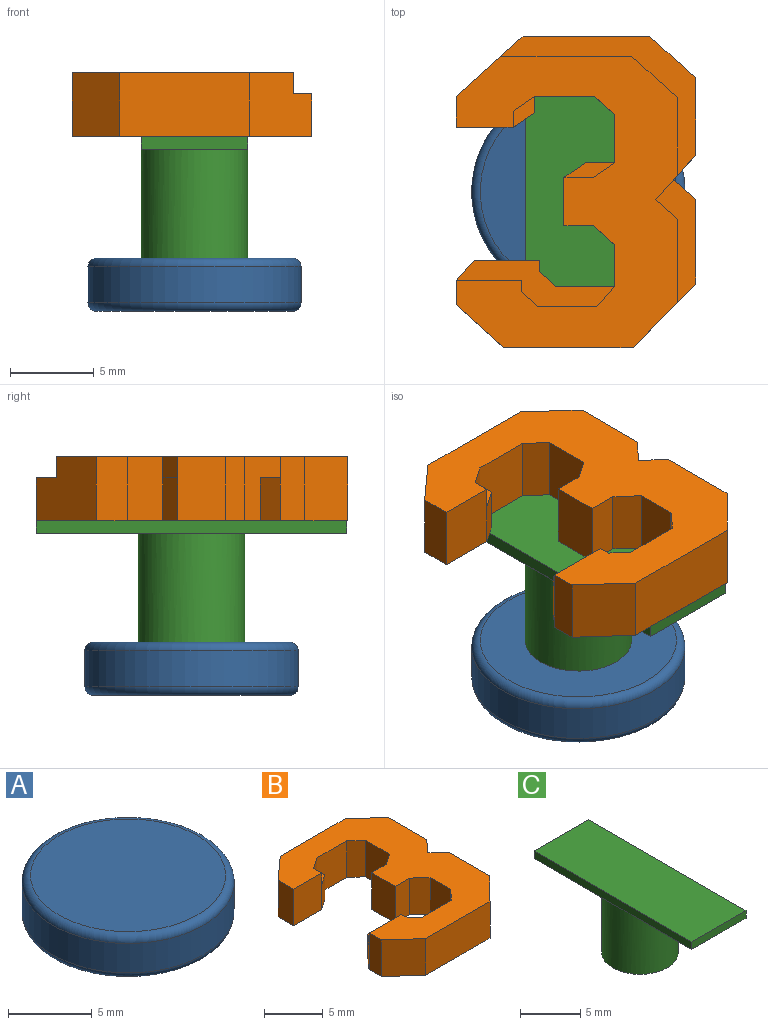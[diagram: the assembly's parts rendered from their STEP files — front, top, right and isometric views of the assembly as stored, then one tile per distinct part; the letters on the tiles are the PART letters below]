
ASSEMBLY  parts=3 mates=3
PART A: 5 faces, bbox 13.7x13.7x3.2 mm
  f0: cylinder r=6.35mm len=12.7mm, axis (0,0,1), area 86.1mm2, adj f3,f4
  f1: plane 11.68x11.68mm, normal (0,0,-1), area 107.2mm2, adj f4
  f2: plane 11.68x11.68mm, normal (0,0,1), area 107.2mm2, adj f3
  f3: torus R=5.84mm, axis (0,0,1), area 30.9mm2, adj f0,f2
  f4: torus R=5.84mm, axis (0,0,1), area 30.9mm2, adj f0,f1
PART B: 50 faces, bbox 14.3x18.5x3.8 mm
  f0: plane 3.88x1.27mm, normal (0,1,0), area 4.9mm2, adj f1,f28,f29,f36
  f1: plane 3.81x1.45mm, normal (-1,0,0), area 5.5mm2, adj f0,f2,f29,f30,f31
  f2: plane 3.81x2.83mm, normal (-0.67,-0.74,0), area 14.5mm2, adj f1,f3,f29,f30
  f3: plane 7.71x3.81mm, normal (0,-1,0), area 29.4mm2, adj f2,f4,f29,f30
  f4: plane 3.81x3.78mm, normal (0.71,-0.7,0), area 18.3mm2, adj f3,f5,f29,f30,f38,f39
  f5: plane 4.94x1.27mm, normal (1,0,0), area 6.3mm2, adj f4,f6,f29,f39
  f6: plane 1.31x1.27mm, normal (0.67,0.74,0), area 2.2mm2, adj f5,f7,f29,f39
  f7: plane 3.81x2.63mm, normal (0.74,-0.67,0), area 7.4mm2, adj f6,f8,f29,f30,f37,f39,f40,f43
  f8: plane 4.62x1.27mm, normal (1,0,0), area 5.9mm2, adj f7,f9,f29,f43
  f9: plane 2.73x2.46mm, normal (0.67,0.74,0), area 4.7mm2, adj f8,f10,f29,f43
  f10: plane 7.8x1.27mm, normal (0,1,0), area 9.9mm2, adj f9,f11,f29,f43
  f11: plane 3.98x3.81mm, normal (-0.67,0.74,0), area 18.1mm2, adj f10,f12,f29,f30,f42,f43
  f12: plane 3.81x1.84mm, normal (-1,0,0), area 7mm2, adj f11,f13,f29,f30
  f13: plane 3.81x3.39mm, normal (0,-1,0), area 12.9mm2, adj f12,f14,f29,f30,f44
  f14: plane 1.27x0.97mm, normal (1,0,0), area 1.2mm2, adj f13,f15,f29,f46
  f15: plane 1.27x1.26mm, normal (0.57,-0.82,0), area 1.9mm2, adj f14,f16,f29,f46
  f16: plane 3.81x3.59mm, normal (0,-1,0), area 13.7mm2, adj f15,f17,f29,f30,f45
  f17: plane 3.81x1.2mm, normal (-0.67,-0.74,0), area 6.2mm2, adj f16,f18,f29,f30
  f18: plane 3.81x2.88mm, normal (-1,0,0), area 11mm2, adj f17,f19,f29,f30,f47
  f19: plane 1.27x1.26mm, normal (-0.57,0.82,0), area 1.9mm2, adj f18,f20,f29,f49
  f20: plane 1.76x1.27mm, normal (0,1,0), area 2.2mm2, adj f19,f21,f29,f49
  f21: plane 3.81x2.86mm, normal (-1,0,0), area 10.9mm2, adj f20,f22,f29,f30,f48
  f22: plane 3.81x1.75mm, normal (0,-1,0), area 6.6mm2, adj f21,f23,f29,f30
  f23: plane 3.81x1.27mm, normal (-0.67,-0.74,0), area 6.5mm2, adj f22,f24,f29,f30
  f24: plane 3.81x2.46mm, normal (-1,0,0), area 9.4mm2, adj f23,f25,f29,f30,f32
  f25: plane 1.27x1.2mm, normal (-0.75,0.66,0), area 2mm2, adj f24,f26,f29,f36
  f26: plane 3.53x1.27mm, normal (0,1,0), area 4.5mm2, adj f25,f27,f29,f36
  f27: plane 1.27x0.98mm, normal (0.66,0.75,0), area 1.7mm2, adj f26,f28,f29,f36
  f28: plane 1.27x0.68mm, normal (1,0,0), area 0.9mm2, adj f0,f27,f29,f36
  f29: plane 17.34x13.21mm, normal (0,0,1), area 119.9mm2, adj f0,f1,f2,f3,f4,f5,f6,f7
  f30: plane 18.53x14.28mm, normal (0,0,-1), area 162.5mm2, adj f1,f2,f3,f4,f7,f11,f12,f13
  f31: plane 2.54x1.21mm, normal (-0.75,0.66,0), area 4.1mm2, adj f1,f30,f35,f36
  f32: plane 3.53x2.54mm, normal (0,1,0), area 9mm2, adj f24,f30,f33,f36
  f33: plane 2.54x0.97mm, normal (0.67,0.74,0), area 3.3mm2, adj f30,f32,f34,f36
  f34: plane 2.54x0.68mm, normal (1,0,0), area 1.7mm2, adj f30,f33,f35,f36
  f35: plane 3.88x2.54mm, normal (0,1,0), area 9.9mm2, adj f30,f31,f34,f36
  f36: plane 9.44x2.75mm, normal (0,0,1), area 11.8mm2, adj f0,f25,f26,f27,f28,f31,f32,f33
  f37: plane 2.54x1.31mm, normal (0.67,0.74,0), area 4.5mm2, adj f7,f30,f38,f39
  f38: plane 5.05x2.54mm, normal (1,0,0), area 12.8mm2, adj f4,f30,f37,f39
  f39: plane 7.32x2.38mm, normal (0,0,1), area 8.2mm2, adj f4,f5,f6,f7,f37,f38
  f40: plane 4.62x2.54mm, normal (1,0,0), area 11.7mm2, adj f7,f30,f41,f43
  f41: plane 2.73x2.54mm, normal (0.67,0.74,0), area 9.3mm2, adj f30,f40,f42,f43
  f42: plane 7.54x2.54mm, normal (0,1,0), area 19.2mm2, adj f11,f30,f41,f43
  f43: plane 11.6x8.27mm, normal (0,0,1), area 19.9mm2, adj f7,f8,f9,f10,f11,f40,f41,f42
  f44: plane 2.54x1.26mm, normal (0.57,-0.82,0), area 3.9mm2, adj f13,f30,f45,f46
  f45: plane 2.54x0.97mm, normal (1,0,0), area 2.5mm2, adj f16,f30,f44,f46
  f46: plane 1.84x1.26mm, normal (0,0,1), area 1.2mm2, adj f14,f15,f44,f45
  f47: plane 2.54x1.76mm, normal (0,1,0), area 4.5mm2, adj f18,f30,f48,f49
  f48: plane 2.54x1.26mm, normal (-0.57,0.82,0), area 3.9mm2, adj f21,f30,f47,f49
  f49: plane 3.02x0.87mm, normal (0,0,1), area 1.5mm2, adj f19,f20,f47,f48
PART C: 9 faces, bbox 6.4x18.5x7.2 mm
  f0: cylinder r=3.17mm len=6.48mm, axis (0,0,-1), area 129.2mm2, adj f1,f2,f8
  f1: plane 6.35x6.35mm, normal (0,0,-1), area 31.7mm2, adj f0
  f2: plane 9.24x6.35mm, normal (0,0,-1), area 42.8mm2, adj f0,f4,f5,f6
  f3: plane 6.35x0.76mm, normal (0,-1,0), area 4.8mm2, adj f4,f6,f7,f8
  f4: plane 18.48x0.76mm, normal (1,0,0), area 14.1mm2, adj f2,f3,f5,f7,f8
  f5: plane 6.35x0.76mm, normal (0,1,0), area 4.8mm2, adj f2,f4,f6,f7
  f6: plane 18.48x0.76mm, normal (-1,0,0), area 14.1mm2, adj f2,f3,f5,f7,f8
  f7: plane 18.48x6.35mm, normal (0,0,1), area 117.3mm2, adj f3,f4,f5,f6
  f8: plane 9.24x6.35mm, normal (0,0,-1), area 42.8mm2, adj f0,f3,f4,f6
PLACE A t=(-4.19,-0.61,-7.66)mm
PLACE B t=(2.44,5.05,-0.42)mm
PLACE C t=(-4.19,-0.61,-7.66)mm
MATE planar B.f30 <-> C.f0  axis (0,0,-1) through (-3.18,-0.66,-0.42)mm
MATE planar B.f42 <-> C.f5  axis (0,1,0) through (-3.71,8.63,0.85)mm
MATE fastened C.f0 <-> A.f0  axis (0,0,-1) through (-4.19,-0.61,-7.66)mm
